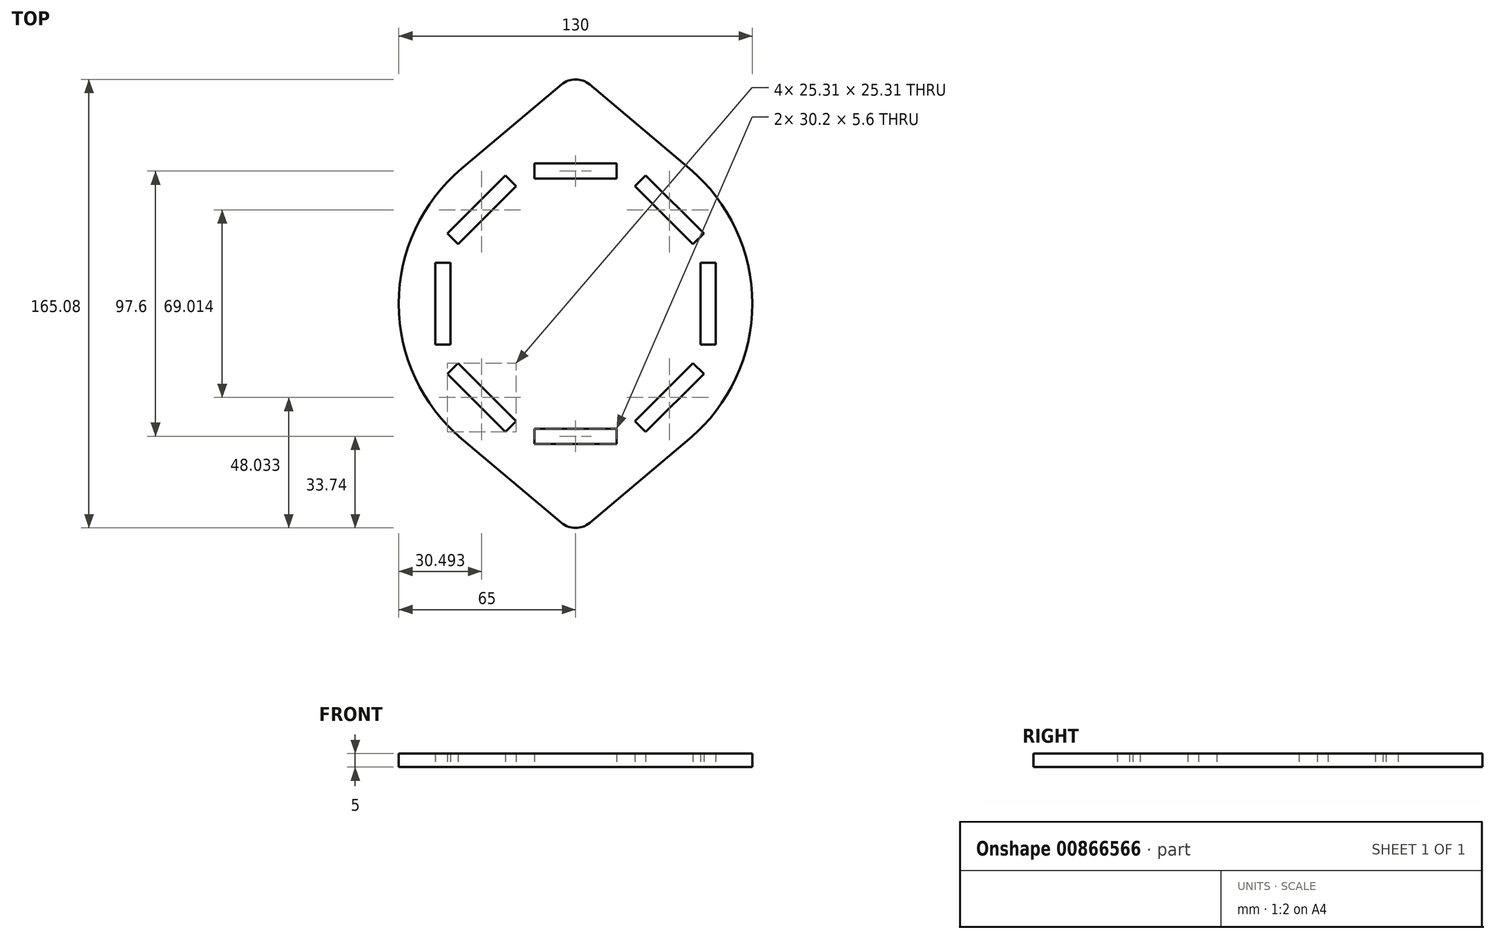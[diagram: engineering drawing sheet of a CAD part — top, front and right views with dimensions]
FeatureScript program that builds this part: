
annotation { "Feature Type Name" : "Feature", "Feature Type Description" : "" }
export const myFeature = defineFeature(function(context is Context, id is Id, definition is map)
    precondition{}
    {
        {
            var Q0;
            Q0=qCreatedBy(makeId("Top.planeOp"),FACE);
            var sketch = newSketch(context, id + "F0", { "sketchPlane" : qUnion([Q0])});
            skCircle(sketch, "E0", {"center": v(0, 0) * mm, "radius": 46 * mm, "construction": true});
            skLineSegment(sketch, "E1", {"start": v(-46, 0) * mm, "end": v(-46, 15.1) * mm});
            skLineSegment(sketch, "E2", {"start": v(-46, 15.1) * mm, "end": v(-51.6, 15.1) * mm});
            skLineSegment(sketch, "E3", {"start": v(-51.6, 15.1) * mm, "end": v(-51.6, 0) * mm});
            skLineSegment(sketch, "E4", {"start": v(-68.94, 0) * mm, "end": v(-11.28, 0) * mm, "construction": true});
            skLineSegment(sketch, "E5.MirrorCS", {"start": v(-51.6, -15.1) * mm, "end": v(-51.6, 0) * mm});
            skLineSegment(sketch, "E6.MirrorCS", {"start": v(-46, 0) * mm, "end": v(-46, -15.1) * mm});
            skLineSegment(sketch, "E7.MirrorCS", {"start": v(-46, -15.1) * mm, "end": v(-51.6, -15.1) * mm});
            skCircle(sketch, "E8", {"center": v(0, 0) * mm, "radius": 65 * mm});
            skLineSegment(sketch, "E9", {"start": v(0, 0) * mm, "end": v(0, 91.08) * mm, "construction": true});
            skLineSegment(sketch, "E10", {"start": v(-5.16, 80.66) * mm, "end": v(-41.88, 49.7) * mm});
            skLineSegment(sketch, "E11.MirrorCS", {"start": v(5.16, 80.66) * mm, "end": v(41.88, 49.7) * mm});
            skPoint(sketch, "E12.visualSharp", {"position": v(0, 85) * mm});
            skArc(sketch, "E12.filletArc", {"start": v(5.16, 80.66) * mm, "mid": v(0, 82.54) * mm, "end": v(-5.16, 80.66) * mm});
            skLineSegment(sketch, "E13.MirrorCS", {"start": v(-5.16, -80.66) * mm, "end": v(-41.88, -49.7) * mm});
            skArc(sketch, "E14.MirrorCS", {"start": v(5.16, -80.66) * mm, "mid": v(0, -82.54) * mm, "end": v(-5.16, -80.66) * mm});
            skLineSegment(sketch, "E15.MirrorCS", {"start": v(5.16, -80.66) * mm, "end": v(41.88, -49.7) * mm});
            skLineSegment(sketch, "E16.1.0", {"start": v(-43.2, -21.85) * mm, "end": v(-47.16, -25.8) * mm});
            skLineSegment(sketch, "E16.1.1", {"start": v(-47.16, -25.8) * mm, "end": v(-36.49, -36.49) * mm});
            skLineSegment(sketch, "E16.1.2", {"start": v(-25.8, -47.16) * mm, "end": v(-36.49, -36.49) * mm});
            skLineSegment(sketch, "E16.1.3", {"start": v(-21.85, -43.2) * mm, "end": v(-25.8, -47.16) * mm});
            skLineSegment(sketch, "E16.1.4", {"start": v(-32.53, -32.53) * mm, "end": v(-21.85, -43.2) * mm});
            skLineSegment(sketch, "E16.1.5", {"start": v(-32.53, -32.53) * mm, "end": v(-43.2, -21.85) * mm});
            skLineSegment(sketch, "E16.2.0", {"start": v(-15.1, -46) * mm, "end": v(-15.1, -51.6) * mm});
            skLineSegment(sketch, "E16.2.1", {"start": v(-15.1, -51.6) * mm, "end": v(0, -51.6) * mm});
            skLineSegment(sketch, "E16.2.2", {"start": v(15.1, -51.6) * mm, "end": v(0, -51.6) * mm});
            skLineSegment(sketch, "E16.2.3", {"start": v(15.1, -46) * mm, "end": v(15.1, -51.6) * mm});
            skLineSegment(sketch, "E16.2.4", {"start": v(0, -46) * mm, "end": v(15.1, -46) * mm});
            skLineSegment(sketch, "E16.2.5", {"start": v(0, -46) * mm, "end": v(-15.1, -46) * mm});
            skLineSegment(sketch, "E17.2.3.0", {"start": v(21.85, -43.2) * mm, "end": v(25.8, -47.16) * mm});
            skLineSegment(sketch, "E17.3.3.0", {"start": v(25.8, -47.16) * mm, "end": v(36.49, -36.49) * mm});
            skLineSegment(sketch, "E17.6.3.0", {"start": v(47.16, -25.8) * mm, "end": v(36.49, -36.49) * mm});
            skLineSegment(sketch, "E17.9.3.0", {"start": v(43.2, -21.85) * mm, "end": v(47.16, -25.8) * mm});
            skLineSegment(sketch, "E17.12.3.0", {"start": v(32.53, -32.53) * mm, "end": v(43.2, -21.85) * mm});
            skLineSegment(sketch, "E17.15.3.0", {"start": v(32.53, -32.53) * mm, "end": v(21.85, -43.2) * mm});
            skLineSegment(sketch, "E17.2.4.0", {"start": v(46, -15.1) * mm, "end": v(51.6, -15.1) * mm});
            skLineSegment(sketch, "E17.3.4.0", {"start": v(51.6, -15.1) * mm, "end": v(51.6, 0) * mm});
            skLineSegment(sketch, "E17.6.4.0", {"start": v(51.6, 15.1) * mm, "end": v(51.6, 0) * mm});
            skLineSegment(sketch, "E17.9.4.0", {"start": v(46, 15.1) * mm, "end": v(51.6, 15.1) * mm});
            skLineSegment(sketch, "E17.12.4.0", {"start": v(46, 0) * mm, "end": v(46, 15.1) * mm});
            skLineSegment(sketch, "E17.15.4.0", {"start": v(46, 0) * mm, "end": v(46, -15.1) * mm});
            skLineSegment(sketch, "E17.2.5.0", {"start": v(43.2, 21.85) * mm, "end": v(47.16, 25.8) * mm});
            skLineSegment(sketch, "E17.3.5.0", {"start": v(47.16, 25.8) * mm, "end": v(36.49, 36.49) * mm});
            skLineSegment(sketch, "E17.6.5.0", {"start": v(25.8, 47.16) * mm, "end": v(36.49, 36.49) * mm});
            skLineSegment(sketch, "E17.9.5.0", {"start": v(21.85, 43.2) * mm, "end": v(25.8, 47.16) * mm});
            skLineSegment(sketch, "E17.12.5.0", {"start": v(32.53, 32.53) * mm, "end": v(21.85, 43.2) * mm});
            skLineSegment(sketch, "E17.15.5.0", {"start": v(32.53, 32.53) * mm, "end": v(43.2, 21.85) * mm});
            skLineSegment(sketch, "E18.2.6.0", {"start": v(15.1, 46) * mm, "end": v(15.1, 51.6) * mm});
            skLineSegment(sketch, "E18.3.6.0", {"start": v(15.1, 51.6) * mm, "end": v(0, 51.6) * mm});
            skLineSegment(sketch, "E18.6.6.0", {"start": v(-15.1, 51.6) * mm, "end": v(0, 51.6) * mm});
            skLineSegment(sketch, "E18.9.6.0", {"start": v(-15.1, 46) * mm, "end": v(-15.1, 51.6) * mm});
            skLineSegment(sketch, "E18.12.6.0", {"start": v(0, 46) * mm, "end": v(-15.1, 46) * mm});
            skLineSegment(sketch, "E18.15.6.0", {"start": v(0, 46) * mm, "end": v(15.1, 46) * mm});
            skLineSegment(sketch, "E18.2.7.0", {"start": v(-21.85, 43.2) * mm, "end": v(-25.8, 47.16) * mm});
            skLineSegment(sketch, "E18.3.7.0", {"start": v(-25.8, 47.16) * mm, "end": v(-36.49, 36.49) * mm});
            skLineSegment(sketch, "E18.6.7.0", {"start": v(-47.16, 25.8) * mm, "end": v(-36.49, 36.49) * mm});
            skLineSegment(sketch, "E18.9.7.0", {"start": v(-43.2, 21.85) * mm, "end": v(-47.16, 25.8) * mm});
            skLineSegment(sketch, "E18.12.7.0", {"start": v(-32.53, 32.53) * mm, "end": v(-43.2, 21.85) * mm});
            skLineSegment(sketch, "E18.15.7.0", {"start": v(-32.53, 32.53) * mm, "end": v(-21.85, 43.2) * mm});
            skSolve(sketch);
        }
        {
            var Q0;
            Q0 = qSketchRegion(id + "F0", true);
            extrude(context, id + "F1", {"entities" : qUnion([Q0]), "depth" : 5 * mm, "offsetDistance" : 25 * mm});
        }
    });
